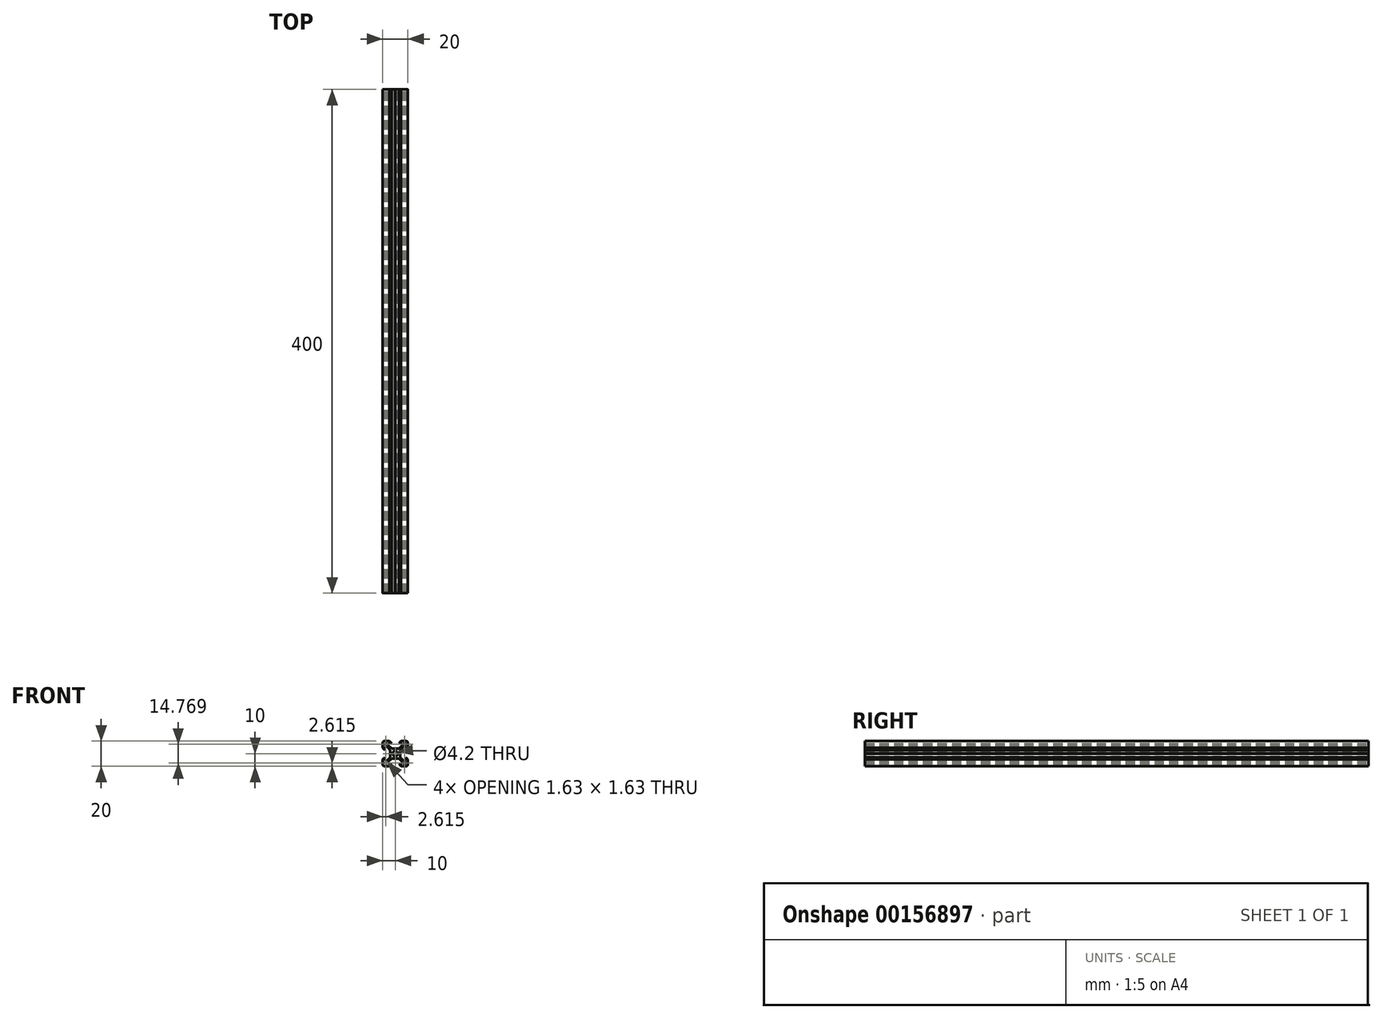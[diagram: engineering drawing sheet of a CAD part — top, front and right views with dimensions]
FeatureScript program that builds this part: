
annotation { "Feature Type Name" : "Feature", "Feature Type Description" : "" }
export const myFeature = defineFeature(function(context is Context, id is Id, definition is map)
    precondition{}
    {
        {
            var Q0;
            Q0=qCreatedBy(makeId("Front.planeOp"),FACE);
            var sketch = newSketch(context, id + "F0", { "sketchPlane" : qUnion([Q0])});
            skArc(sketch, "E0", {"start": v(-8.5, 10) * mm, "mid": v(-9.56, 9.56) * mm, "end": v(-10, 8.5) * mm});
            skLineSegment(sketch, "E1", {"start": v(-10, 8.5) * mm, "end": v(-10, 4.64) * mm});
            skLineSegment(sketch, "E2", {"start": v(-10, 4.64) * mm, "end": v(-8.2, 2.84) * mm});
            skLineSegment(sketch, "E3", {"start": v(-8.2, 5.5) * mm, "end": v(-8.2, 2.84) * mm});
            skLineSegment(sketch, "E4", {"start": v(-8.2, 5.5) * mm, "end": v(-6.56, 5.5) * mm});
            skLineSegment(sketch, "E5", {"start": v(-6.56, 5.5) * mm, "end": v(-3.9, 2.84) * mm});
            skLineSegment(sketch, "E6", {"start": v(-3.9, 2.84) * mm, "end": v(-3.9, 0.2) * mm});
            skLineSegment(sketch, "E7", {"start": v(-3.9, 0.2) * mm, "end": v(-3.7, 0) * mm});
            skLineSegment(sketch, "E8", {"start": v(-3.9, -0.2) * mm, "end": v(-3.7, 0) * mm});
            skLineSegment(sketch, "E9", {"start": v(-3.9, -2.84) * mm, "end": v(-3.9, -0.2) * mm});
            skLineSegment(sketch, "E10", {"start": v(-6.56, -5.5) * mm, "end": v(-3.9, -2.84) * mm});
            skLineSegment(sketch, "E11", {"start": v(-8.2, -5.5) * mm, "end": v(-6.56, -5.5) * mm});
            skLineSegment(sketch, "E12", {"start": v(-8.2, -5.5) * mm, "end": v(-8.2, -2.84) * mm});
            skLineSegment(sketch, "E13", {"start": v(-10, -4.64) * mm, "end": v(-8.2, -2.84) * mm});
            skLineSegment(sketch, "E14", {"start": v(-10, -8.5) * mm, "end": v(-10, -4.64) * mm});
            skArc(sketch, "E15", {"start": v(-10, -8.5) * mm, "mid": v(-9.56, -9.56) * mm, "end": v(-8.5, -10) * mm});
            skLineSegment(sketch, "E16", {"start": v(-8.5, -10) * mm, "end": v(-4.64, -10) * mm});
            skLineSegment(sketch, "E17", {"start": v(-4.64, -10) * mm, "end": v(-2.84, -8.2) * mm});
            skLineSegment(sketch, "E18", {"start": v(-2.84, -8.2) * mm, "end": v(-5.5, -8.2) * mm});
            skLineSegment(sketch, "E19", {"start": v(-5.5, -8.2) * mm, "end": v(-5.5, -6.56) * mm});
            skLineSegment(sketch, "E20", {"start": v(-5.5, -6.56) * mm, "end": v(-2.84, -3.9) * mm});
            skLineSegment(sketch, "E21", {"start": v(-0.2, -3.9) * mm, "end": v(-2.84, -3.9) * mm});
            skLineSegment(sketch, "E22", {"start": v(-0.2, -3.9) * mm, "end": v(0, -3.7) * mm});
            skLineSegment(sketch, "E23", {"start": v(0.2, -3.9) * mm, "end": v(0, -3.7) * mm});
            skLineSegment(sketch, "E24", {"start": v(0.2, -3.9) * mm, "end": v(2.84, -3.9) * mm});
            skLineSegment(sketch, "E25", {"start": v(5.5, -6.56) * mm, "end": v(2.84, -3.9) * mm});
            skLineSegment(sketch, "E26", {"start": v(5.5, -8.2) * mm, "end": v(5.5, -6.56) * mm});
            skLineSegment(sketch, "E27", {"start": v(2.84, -8.2) * mm, "end": v(5.5, -8.2) * mm});
            skLineSegment(sketch, "E28", {"start": v(4.64, -10) * mm, "end": v(2.84, -8.2) * mm});
            skLineSegment(sketch, "E29", {"start": v(8.5, -10) * mm, "end": v(4.64, -10) * mm});
            skArc(sketch, "E30", {"start": v(8.5, -10) * mm, "mid": v(9.56, -9.56) * mm, "end": v(10, -8.5) * mm});
            skLineSegment(sketch, "E31", {"start": v(10, -8.5) * mm, "end": v(10, -4.64) * mm});
            skLineSegment(sketch, "E32", {"start": v(10, -4.64) * mm, "end": v(8.2, -2.84) * mm});
            skLineSegment(sketch, "E33", {"start": v(8.2, -5.5) * mm, "end": v(8.2, -2.84) * mm});
            skLineSegment(sketch, "E34", {"start": v(8.2, -5.5) * mm, "end": v(6.56, -5.5) * mm});
            skLineSegment(sketch, "E35", {"start": v(6.56, -5.5) * mm, "end": v(3.9, -2.84) * mm});
            skLineSegment(sketch, "E36", {"start": v(3.9, -2.84) * mm, "end": v(3.9, -0.2) * mm});
            skLineSegment(sketch, "E37", {"start": v(3.9, -0.2) * mm, "end": v(3.7, 0) * mm});
            skLineSegment(sketch, "E38", {"start": v(3.9, 0.2) * mm, "end": v(3.7, 0) * mm});
            skLineSegment(sketch, "E39", {"start": v(3.9, 2.84) * mm, "end": v(3.9, 0.2) * mm});
            skLineSegment(sketch, "E40", {"start": v(6.56, 5.5) * mm, "end": v(3.9, 2.84) * mm});
            skLineSegment(sketch, "E41", {"start": v(8.2, 5.5) * mm, "end": v(6.56, 5.5) * mm});
            skLineSegment(sketch, "E42", {"start": v(8.2, 5.5) * mm, "end": v(8.2, 2.84) * mm});
            skLineSegment(sketch, "E43", {"start": v(10, 4.64) * mm, "end": v(8.2, 2.84) * mm});
            skLineSegment(sketch, "E44", {"start": v(10, 8.5) * mm, "end": v(10, 4.64) * mm});
            skArc(sketch, "E45", {"start": v(10, 8.5) * mm, "mid": v(9.56, 9.56) * mm, "end": v(8.5, 10) * mm});
            skLineSegment(sketch, "E46", {"start": v(8.5, 10) * mm, "end": v(4.64, 10) * mm});
            skLineSegment(sketch, "E47", {"start": v(4.64, 10) * mm, "end": v(2.84, 8.2) * mm});
            skLineSegment(sketch, "E48", {"start": v(2.84, 8.2) * mm, "end": v(5.5, 8.2) * mm});
            skLineSegment(sketch, "E49", {"start": v(5.5, 8.2) * mm, "end": v(5.5, 6.56) * mm});
            skLineSegment(sketch, "E50", {"start": v(5.5, 6.56) * mm, "end": v(2.84, 3.9) * mm});
            skLineSegment(sketch, "E51", {"start": v(0.2, 3.9) * mm, "end": v(2.84, 3.9) * mm});
            skLineSegment(sketch, "E52", {"start": v(0.2, 3.9) * mm, "end": v(0, 3.7) * mm});
            skLineSegment(sketch, "E53", {"start": v(-0.2, 3.9) * mm, "end": v(0, 3.7) * mm});
            skLineSegment(sketch, "E54", {"start": v(-0.2, 3.9) * mm, "end": v(-2.84, 3.9) * mm});
            skLineSegment(sketch, "E55", {"start": v(-5.5, 6.56) * mm, "end": v(-2.84, 3.9) * mm});
            skLineSegment(sketch, "E56", {"start": v(-5.5, 8.2) * mm, "end": v(-5.5, 6.56) * mm});
            skLineSegment(sketch, "E57", {"start": v(-2.84, 8.2) * mm, "end": v(-5.5, 8.2) * mm});
            skLineSegment(sketch, "E58", {"start": v(-4.64, 10) * mm, "end": v(-2.84, 8.2) * mm});
            skLineSegment(sketch, "E59", {"start": v(-8.5, 10) * mm, "end": v(-4.64, 10) * mm});
            skCircle(sketch, "E60", {"center": v(0, 0) * mm, "radius": 2.1 * mm});
            skLineSegment(sketch, "E61", {"start": v(-6.57, 8.2) * mm, "end": v(-8.2, 8.2) * mm});
            skLineSegment(sketch, "E62", {"start": v(-6.57, 8.2) * mm, "end": v(-6.57, 7.63) * mm});
            skLineSegment(sketch, "E63", {"start": v(-7.63, 6.57) * mm, "end": v(-6.57, 7.63) * mm});
            skLineSegment(sketch, "E64", {"start": v(-8.2, 6.57) * mm, "end": v(-7.63, 6.57) * mm});
            skLineSegment(sketch, "E65", {"start": v(-8.2, 8.2) * mm, "end": v(-8.2, 6.57) * mm});
            skLineSegment(sketch, "E66", {"start": v(8.2, 8.2) * mm, "end": v(8.2, 6.57) * mm});
            skLineSegment(sketch, "E67", {"start": v(8.2, 6.57) * mm, "end": v(7.63, 6.57) * mm});
            skLineSegment(sketch, "E68", {"start": v(7.63, 6.57) * mm, "end": v(6.57, 7.63) * mm});
            skLineSegment(sketch, "E69", {"start": v(6.57, 8.2) * mm, "end": v(6.57, 7.63) * mm});
            skLineSegment(sketch, "E70", {"start": v(6.57, 8.2) * mm, "end": v(8.2, 8.2) * mm});
            skLineSegment(sketch, "E71", {"start": v(-8.2, -8.2) * mm, "end": v(-8.2, -6.57) * mm});
            skLineSegment(sketch, "E72", {"start": v(-8.2, -6.57) * mm, "end": v(-7.63, -6.57) * mm});
            skLineSegment(sketch, "E73", {"start": v(-7.63, -6.57) * mm, "end": v(-6.57, -7.63) * mm});
            skLineSegment(sketch, "E74", {"start": v(-6.57, -8.2) * mm, "end": v(-6.57, -7.63) * mm});
            skLineSegment(sketch, "E75", {"start": v(-6.57, -8.2) * mm, "end": v(-8.2, -8.2) * mm});
            skLineSegment(sketch, "E76", {"start": v(6.57, -8.2) * mm, "end": v(8.2, -8.2) * mm});
            skLineSegment(sketch, "E77", {"start": v(6.57, -8.2) * mm, "end": v(6.57, -7.63) * mm});
            skLineSegment(sketch, "E78", {"start": v(7.63, -6.57) * mm, "end": v(6.57, -7.63) * mm});
            skLineSegment(sketch, "E79", {"start": v(8.2, -6.57) * mm, "end": v(7.63, -6.57) * mm});
            skLineSegment(sketch, "E80", {"start": v(8.2, -8.2) * mm, "end": v(8.2, -6.57) * mm});
            skSolve(sketch);
        }
        {
            var Q0;
            Q0=makeQuery(id+"F0.imprint","IMPRINT",FACE,{"disambiguationData":[TD([[makeQuery(id+"F0.imprint","IMPRINT",EDGE,{"derivedFrom":sQuery(id+"F0.wireOp",EDGE,"E0")}),1.0]])]});
            extrude(context, id + "F1", {"entities" : qUnion([Q0]), "depth" : 400 * mm});
        }
    });
